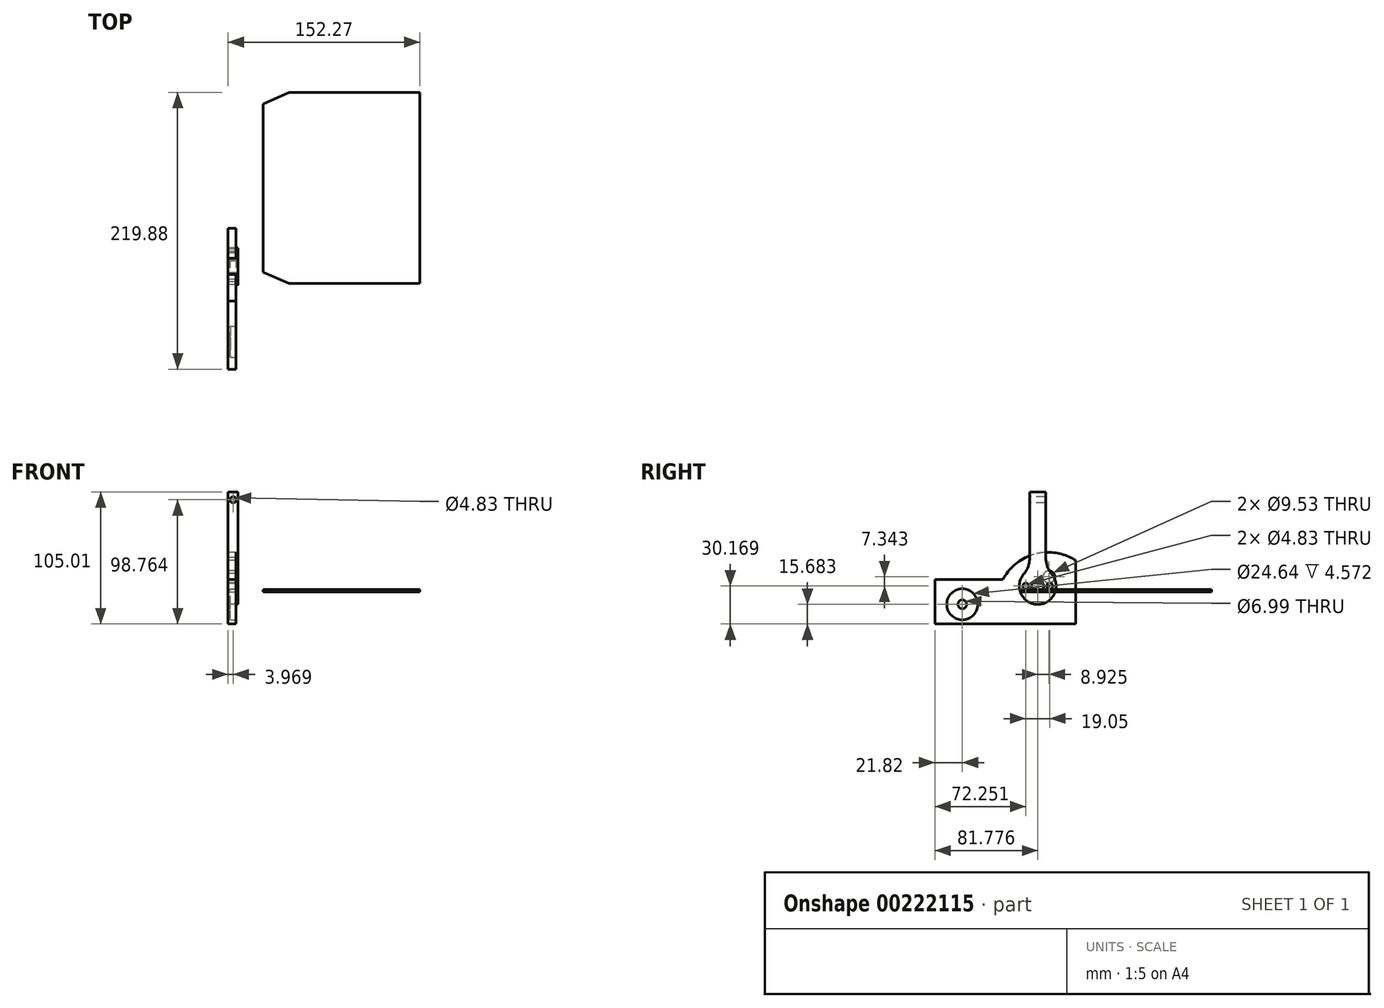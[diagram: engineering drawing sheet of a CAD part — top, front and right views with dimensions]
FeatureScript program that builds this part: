
annotation { "Feature Type Name" : "Feature", "Feature Type Description" : "" }
export const myFeature = defineFeature(function(context is Context, id is Id, definition is map)
    precondition{}
    {
        {
            var Q0;
            Q0=qCreatedBy(makeId("Right.planeOp"),FACE);
            var sketch = newSketch(context, id + "F0", { "sketchPlane" : qUnion([Q0])});
            skLineSegment(sketch, "E0.bottom", {"start": v(-42.04, 79.53) * mm, "end": v(-54.74, 79.53) * mm});
            skLineSegment(sketch, "E0.top", {"start": v(-42.04, 9.68) * mm, "end": v(-54.74, 9.68) * mm});
            skLineSegment(sketch, "E0.left", {"start": v(-42.04, 79.53) * mm, "end": v(-42.04, 9.68) * mm});
            skLineSegment(sketch, "E0.right", {"start": v(-54.74, 79.53) * mm, "end": v(-54.74, 9.68) * mm});
            skCircle(sketch, "E1", {"center": v(-48.4, 4.69) * mm, "radius": 14.6 * mm});
            skPoint(sketch, "E1.centerSnap0", {"position": v(-48.4, 9.68) * mm});
            skLineSegment(sketch, "E2", {"start": v(-48.4, 100.91) * mm, "end": v(-48.4, 79.53) * mm});
            skArc(sketch, "E3", {"start": v(-60.4, 13) * mm, "mid": v(-56.16, 19.93) * mm, "end": v(-54.74, 27.92) * mm});
            skArc(sketch, "E4.MirrorCS", {"start": v(-36.39, 13) * mm, "mid": v(-40.63, 19.93) * mm, "end": v(-42.04, 27.92) * mm});
            skSolve(sketch);
        }
        {
            var Q0;
            Q0 = qSketchRegion(id + "F0", true);
            var Q1;
            {var subQ0=sQuery(id+"F0.wireOp",EDGE,"E0.top");Q1=makeQuery(id+"F0.imprint","IMPRINT",FACE,{"disambiguationData":[TD([[makeQuery(id+"F0.imprint","IMPRINT",EDGE,{"derivedFrom":subQ0}),-1.0]])]});}
            extrude(context, id + "F1", {"entities" : qUnion([Q0, Q1]), "depth" : 7.94 * mm});
        }
        {
            var Q0;
            Q0=makeQuery(id+"F1.opExtrude","SWEPT_FACE",FACE,{"disambiguationData":[OSD([sQuery(id+"F0.wireOp",EDGE,"E0.right")])]});
            var sketch = newSketch(context, id + "F2", { "sketchPlane" : qUnion([Q0])});
            skCircle(sketch, "E5", {"center": v(3.97, 73.28) * mm, "radius": 2.41 * mm});
            skPoint(sketch, "E5.centerSnap0", {"position": v(3.97, 79.53) * mm});
            skSolve(sketch);
        }
        {
            var Q0;
            Q0 = qSketchRegion(id + "F2", true);
            var Q1;
            Q1=makeQuery(id+"F1.opExtrude","SWEPT_FACE",FACE,{"disambiguationData":[OSD([sQuery(id+"F0.wireOp",EDGE,"E0.left")])]});
            extrude(context, id + "F3", {"entities" : qUnion([Q0]), "operationType" : NewBodyOperationType.REMOVE, "endBound" : BoundingType.UP_TO_SURFACE, "oppositeDirection" : true, "endBoundEntityFace" : qUnion([Q1]), "depth" : 25.4 * mm});
        }
        {
            var Q0;
            Q0=makeQuery(id+"F1.opExtrude","CAP_FACE",FACE,{"disambiguationData":[OSD([sQuery(id+"F0.wireOp",EDGE,"E0.bottom"),sQuery(id+"F0.wireOp",EDGE,"E0.left"),sQuery(id+"F0.wireOp",EDGE,"E0.right"),sQuery(id+"F0.wireOp",EDGE,"E1")])],"isStart":false});
            var sketch = newSketch(context, id + "F4", { "sketchPlane" : qUnion([Q0])});
            skCircle(sketch, "E6", {"center": v(-48.4, 4.69) * mm, "radius": 4.76 * mm});
            skLineSegment(sketch, "E7", {"start": v(-48.4, 4.69) * mm, "end": v(-57.92, 4.69) * mm});
            skCircle(sketch, "E8", {"center": v(-57.92, 4.69) * mm, "radius": 2.41 * mm});
            skLineSegment(sketch, "E9", {"start": v(-48.4, 4.69) * mm, "end": v(-48.4, 8.03) * mm});
            skCircle(sketch, "E10.MirrorC", {"center": v(-38.87, 4.69) * mm, "radius": 2.41 * mm});
            skSolve(sketch);
        }
        {
            var Q0;
            Q0 = qSketchRegion(id + "F4", true);
            var Q1;
            Q1=makeQuery(id+"F1.opExtrude","CAP_FACE",FACE,{"disambiguationData":[OSD([sQuery(id+"F0.wireOp",EDGE,"E0.bottom"),sQuery(id+"F0.wireOp",EDGE,"E0.left"),sQuery(id+"F0.wireOp",EDGE,"E0.right"),sQuery(id+"F0.wireOp",EDGE,"E1")])],"isStart":true});
            extrude(context, id + "F5", {"entities" : qUnion([Q0]), "operationType" : NewBodyOperationType.REMOVE, "endBound" : BoundingType.UP_TO_SURFACE, "oppositeDirection" : true, "endBoundEntityFace" : qUnion([Q1]), "depth" : 25.4 * mm});
        }
        {
            var Q0;
            Q0=qCreatedBy(makeId("Right.planeOp"),FACE);
            var sketch = newSketch(context, id + "F6", { "sketchPlane" : qUnion([Q0])});
            skLineSegment(sketch, "E11.bottom", {"start": v(-130.17, -25.48) * mm, "end": v(-18.23, -25.48) * mm});
            skLineSegment(sketch, "E11.top", {"start": v(-130.17, 9.8) * mm, "end": v(-18.23, 9.8) * mm});
            skLineSegment(sketch, "E11.left", {"start": v(-130.17, -25.48) * mm, "end": v(-130.17, 9.8) * mm});
            skLineSegment(sketch, "E11.right", {"start": v(-18.23, -25.48) * mm, "end": v(-18.23, 9.8) * mm});
            skCircle(sketch, "E12", {"center": v(-39.47, 12.03) * mm, "radius": 4.76 * mm});
            skLineSegment(sketch, "E13", {"start": v(-18.23, 9.8) * mm, "end": v(-18.23, 25) * mm});
            skArc(sketch, "E14", {"start": v(-18.23, 25) * mm, "mid": v(-50.54, 30.15) * mm, "end": v(-76.15, 9.8) * mm});
            skSolve(sketch);
        }
        {
            var Q0;
            Q0 = qSketchRegion(id + "F6", true);
            extrude(context, id + "F7", {"entities" : qUnion([Q0]), "depth" : 6.35 * mm});
        }
        {
            var Q0;
            Q0=qCreatedBy(makeId("Top.planeOp"),FACE);
            var sketch = newSketch(context, id + "F8", { "sketchPlane" : qUnion([Q0])});
            skLineSegment(sketch, "E15.0", {"start": v(152.27, -62.15) * mm, "end": v(152.27, 89.71) * mm});
            skLineSegment(sketch, "E15.1", {"start": v(48.33, 89.71) * mm, "end": v(27.79, 80.62) * mm});
            skLineSegment(sketch, "E15.2", {"start": v(27.79, 80.62) * mm, "end": v(27.79, -53.06) * mm});
            skLineSegment(sketch, "E15.3", {"start": v(152.27, 89.71) * mm, "end": v(48.33, 89.71) * mm});
            skLineSegment(sketch, "E15.4", {"start": v(48.33, -62.15) * mm, "end": v(27.79, -53.06) * mm});
            skLineSegment(sketch, "E15.5", {"start": v(48.33, -62.15) * mm, "end": v(152.27, -62.15) * mm});
            skSolve(sketch);
        }
        {
            var Q0;
            Q0 = qSketchRegion(id + "F8", true);
            extrude(context, id + "F9", {"entities" : qUnion([Q0]), "depth" : 1.9 * mm});
        }
        {
            var Q0;
            Q0=makeQuery(id+"F7.opExtrude","CAP_FACE",FACE,{"disambiguationData":[OSD([sQuery(id+"F6.wireOp",EDGE,"E11.bottom"),sQuery(id+"F6.wireOp",EDGE,"E11.top"),sQuery(id+"F6.wireOp",EDGE,"E11.left"),sQuery(id+"F6.wireOp",EDGE,"E11.right"),sQuery(id+"F6.wireOp",EDGE,"tOpDGpcQ-ZqUu-kMSO-o1PP-Ui9w3wniOQ4p"),sQuery(id+"F6.wireOp",EDGE,"gyx3YZop-8Wu9-NbWH-M7fe-Q5tytAtaav37"),sQuery(id+"F6.wireOp",EDGE,"RZZRI2l7-G0yX-OVD0-Iqz7-1asLmys1Y3XI"),sQuery(id+"F6.wireOp",EDGE,"E12")])],"isStart":false});
            var sketch = newSketch(context, id + "F10", { "sketchPlane" : qUnion([Q0])});
            skCircle(sketch, "E16", {"center": v(-108.35, -9.8) * mm, "radius": 12.32 * mm});
            skSolve(sketch);
        }
        {
            var Q0;
            Q0 = qSketchRegion(id + "F10", true);
            var Q1;
            Q1=makeQuery(id+"F7.opExtrude","CAP_FACE",FACE,{"disambiguationData":[OSD([sQuery(id+"F6.wireOp",EDGE,"E11.bottom"),sQuery(id+"F6.wireOp",EDGE,"E11.top"),sQuery(id+"F6.wireOp",EDGE,"E11.left"),sQuery(id+"F6.wireOp",EDGE,"E11.right"),sQuery(id+"F6.wireOp",EDGE,"E12"),sQuery(id+"F6.wireOp",EDGE,"E13"),sQuery(id+"F6.wireOp",EDGE,"E14")])],"isStart":true});
            extrude(context, id + "F11", {"entities" : qUnion([Q0]), "operationType" : NewBodyOperationType.REMOVE, "oppositeDirection" : true, "endBoundEntityFace" : qUnion([Q1]), "depth" : 4.57 * mm});
        }
        {
            var Q0;
            Q0=makeQuery(id+"F11.boolean.opBoolean","COPY",FACE,{"derivedFrom":makeQuery(id+"F11.opExtrude","CAP_FACE",FACE,{"disambiguationData":[OSD([sQuery(id+"F10.wireOp",EDGE,"E16")])],"isStart":false})});
            var sketch = newSketch(context, id + "F12", { "sketchPlane" : qUnion([Q0])});
            skCircle(sketch, "E17", {"center": v(-108.35, -9.8) * mm, "radius": 3.5 * mm});
            skSolve(sketch);
        }
        {
            var Q0;
            Q0 = qSketchRegion(id + "F12", true);
            var Q1;
            Q1=makeQuery(id+"F7.opExtrude","CAP_FACE",FACE,{"disambiguationData":[OSD([sQuery(id+"F6.wireOp",EDGE,"E11.bottom"),sQuery(id+"F6.wireOp",EDGE,"E11.top"),sQuery(id+"F6.wireOp",EDGE,"E11.left"),sQuery(id+"F6.wireOp",EDGE,"E11.right"),sQuery(id+"F6.wireOp",EDGE,"E12"),sQuery(id+"F6.wireOp",EDGE,"E13"),sQuery(id+"F6.wireOp",EDGE,"E14")])],"isStart":true});
            extrude(context, id + "F13", {"entities" : qUnion([Q0]), "operationType" : NewBodyOperationType.REMOVE, "endBound" : BoundingType.UP_TO_SURFACE, "oppositeDirection" : true, "endBoundEntityFace" : qUnion([Q1]), "depth" : 25.4 * mm});
        }
    });
